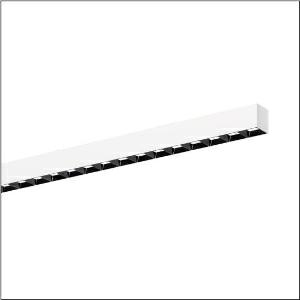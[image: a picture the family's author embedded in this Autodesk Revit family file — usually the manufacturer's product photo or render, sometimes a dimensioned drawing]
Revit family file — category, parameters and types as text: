
# Revit family: silica_r__21_51mx24dc3awb_4576
name_source: partatom
category: Lighting Fixtures
units: mm (PartAtom-declared; Revit-internal decimal feet)

## family parameters
Cut with Voids When Loaded = No
Host = Face
Light Source = No
Part Type = Normal
Room Calculation Point = No
Round Connector Dimension = Use Diameter
Shared = No

## types (1)
- --- (1 x LED, 10800 lm, 79 W, 3000K)
    Apparent Load = 79 VA
    CIE Flux Codes = 74 94 99 100 100
    Color Rendering = 80
    Color Temperature = 3000K
    Default Elevation = 1800 mm
    Description = Silica® 21, office luminaire, primary light control with darklight reflector, of PMMA, black, CAT 2 (L<= 3000cd/m²), light emission: direct distribution, primary light characteristic: asymmetric, installation type: surface-mounted, LED, rated luminous flux: 10.800lm, luminous efficacy: 137lm/W, light colour: 830, colour temperature: 3000K, with terminal, 3+2-pole, max. 2.5mm², mains connection: 220..240V, AC, 50/60Hz, rated input power: 79W, luminaire housing, of aluminium, traffic white (RAL 9016), length: 3.004mm, width: 53mm, height: 53mm, protection rating (complete): IP20, insulation class (complete): insulation class I (protective earthing), certification: CE, permissible operating ambient temperature: 0..+35°C, standard: EN 50419, packaging unit: 1 piece
    Height = 0 mm  [stored 0 ft]
    Lamp = 1 x LED
    Lamp Light Flux = 10800 lm
    Lamp Power = 79 W
    Lamp count = 1
    Length = 3004 mm
    Luminous efficacy = 137 lm/W
    Manufacturer = Siteco
    ModVariant = No
    Model = 51MX24DC3AWB
    Mounting Place = Ceiling
    Mounting Type = Recessed
    Number of Poles = 1
    OnlyDefault = Yes
    Power Factor = 1
    Product Name = Silica® 21
    Product group = office luminaire | ceiling recessed
    ProductGroupID = 401
    Protection Class = Protection class I
    Protection Degree = IP 20
    RLX_Detail_Level = 1
    RLX_Emergency_Light_Flux = 0 lm
    RLX_Emergency_Type = 0
    RLX_Emergency_Type_DB = No
    RlxData = <blob elided: 63401 chars, md5=8411a589>
    Socket = socket
    Standby Power = 0 W
    System Light Flux = 10800 lm
    System Power = 79 W
    Type Comments = factory setting: luminous flux: 100 % | dim-lin: 254 | 448 mA
    Type Image = l_1297779.jpg
    URL = http://relux.com
    VarID = @adj_053771
    Voltage = 0 V
    Weight = 0.00 kg
    Width = 53 mm

note: [stored X ft] marks values corroborated as IEEE doubles in the binary element streams (Revit-internal decimal feet)

## geometry (parser evidence)
native form markers: Blend x4, Sweep x11
no freeform markers — native parametric forms only
